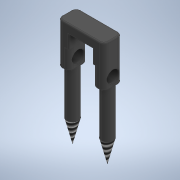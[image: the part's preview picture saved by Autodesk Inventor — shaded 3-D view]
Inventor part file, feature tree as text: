
AUTODESK INVENTOR PART (.ipt)
format: ipt  version: 2022 (Build 260153000, 153)  size: 418,304 bytes
history: native  units: mm
features: fillet x7, sketch x5, extrude x4, plane x2, thread x2, revolve x1, mirror x1
ambient origin geometry x8: Origin, YZ Plane, XZ Plane, XY Plane, X Axis, Y Axis, Z Axis, Center Point
bodies: Solid1 (feature_tree)
feature tree (22):
  sketch  "Sketch1"  dims[d2=8.0mm d3=8.0mm]
  plane  "Work Plane1"
  sketch  "Sketch2"  dims[d11=20.0mm d12=0.0mm d13=20.0mm d14=0.0mm]
  extrude  "Extrusion3"  Depth=8.0mm
  extrude  "Extrusion4"  Depth=20.0mm TaperAngle=0.0deg
  plane  "Work Plane2"
  revolve  "Revolution1"  [1 undecoded]
  fillet  "Fillet1"  Radius=2.441657mm
  fillet  "Fillet2"  [1 undecoded]
  mirror  "Mirror1"
  extrude  "Extrusion5"  Depth=0.5mm
  fillet  "Fillet3"  Radius=10.0mm
  fillet  "Fillet4"  Radius=2.0mm
  fillet  "Fillet5"  Radius=0.2mm
  fillet  "Fillet6"  Radius=0.5mm
  thread  "Thread1"  [1 undecoded]
  thread  "Thread2"  [1 undecoded]
  extrude  "Extrusion6"  Depth=10.0mm
  fillet  "Fillet7"  Radius=10.0mm
  sketch  "Sketch3"  dims[d15=-2.5mm d17=10.0mm d18=2.441657mm d19=90.0deg]
  sketch  "Sketch4"  dims[d20=2.5mm d21=2.5mm d22=10.0mm d23=0.0mm d24=2.0mm d25=0.2mm d26=0.5mm d27=0.5mm d28=23.2mm d29=0.0mm]
  sketch  "Sketch5"  dims[d30=23.2mm d31=0.0mm d32=10.0mm d33=10.0mm d34=10.0mm d35=6.0mm d36=10.0mm d37=0.0mm d38=0.5mm]
note: 4 required parameter values undecoded (feature->parameter linkage not recoverable at this tier; creation-order binding heuristic only, values carry confidence <= 0.55)